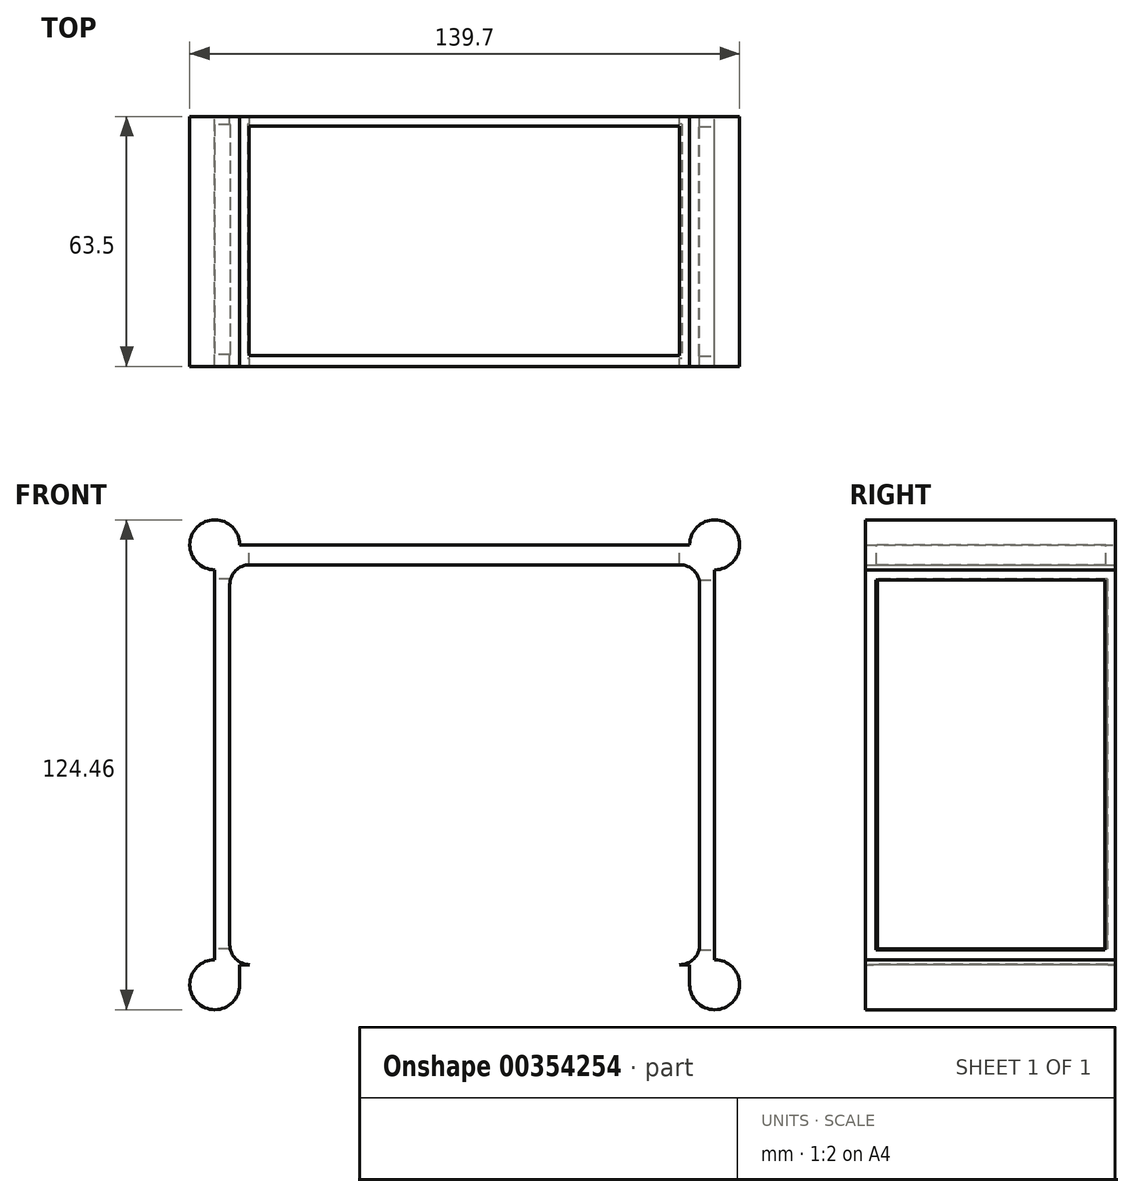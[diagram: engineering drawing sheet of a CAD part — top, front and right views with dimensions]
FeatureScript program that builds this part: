
annotation { "Feature Type Name" : "Feature", "Feature Type Description" : "" }
export const myFeature = defineFeature(function(context is Context, id is Id, definition is map)
    precondition{}
    {
        {
            var Q0;
            Q0=qCreatedBy(makeId("Front.planeOp"),FACE);
            var sketch = newSketch(context, id + "F0", { "sketchPlane" : qUnion([Q0])});
            skLineSegment(sketch, "E0", {"start": v(-62.04, -39.82) * mm, "end": v(64.96, -39.82) * mm});
            skCircle(sketch, "E1", {"center": v(-62.04, -39.82) * mm, "radius": 6.35 * mm});
            skCircle(sketch, "E2", {"center": v(64.96, -39.82) * mm, "radius": 6.35 * mm});
            skLineSegment(sketch, "E3", {"start": v(-62.04, -39.82) * mm, "end": v(-62.04, 71.94) * mm});
            skLineSegment(sketch, "E4", {"start": v(64.96, -39.82) * mm, "end": v(64.96, 71.94) * mm});
            skLineSegment(sketch, "E5", {"start": v(-62.04, 71.94) * mm, "end": v(64.96, 71.94) * mm});
            skCircle(sketch, "E6", {"center": v(-62.04, 71.94) * mm, "radius": 6.35 * mm});
            skCircle(sketch, "E7", {"center": v(64.96, 71.94) * mm, "radius": 6.35 * mm});
            skPoint(sketch, "E8.middle", {"position": v(0, 0) * mm});
            skPoint(sketch, "E9.middle", {"position": v(56.68, 68.54) * mm});
            skLineSegment(sketch, "E10.bottom", {"start": v(-58.23, 66.86) * mm, "end": v(61.15, 66.86) * mm});
            skLineSegment(sketch, "E10.top", {"start": v(-58.23, -34.74) * mm, "end": v(61.15, -34.74) * mm});
            skLineSegment(sketch, "E10.left", {"start": v(-58.23, 66.86) * mm, "end": v(-58.23, -34.74) * mm});
            skLineSegment(sketch, "E10.right", {"start": v(61.15, 66.86) * mm, "end": v(61.15, -34.74) * mm});
            skSolve(sketch);
        }
        {
            var Q0;
            Q0 = qSketchRegion(id + "F0", true);
            extrude(context, id + "F1", {"entities" : qUnion([Q0]), "depth" : 63.5 * mm});
        }
        {
            var Q0;
            Q0=makeQuery(id+"F1.opExtrude","SWEPT_FACE",FACE,{"disambiguationData":[OSD([sQuery(id+"F0.wireOp",EDGE,"E0")])]});
            var sketch = newSketch(context, id + "F2", { "sketchPlane" : qUnion([Q0])});
            skLineSegment(sketch, "E11.bottom", {"start": v(-53.74, 61.5) * mm, "end": v(56.64, 61.5) * mm});
            skLineSegment(sketch, "E11.top", {"start": v(-53.74, 1.95) * mm, "end": v(56.64, 1.95) * mm});
            skLineSegment(sketch, "E11.left", {"start": v(-53.74, 61.5) * mm, "end": v(-53.74, 1.95) * mm});
            skLineSegment(sketch, "E11.right", {"start": v(56.64, 61.5) * mm, "end": v(56.64, 1.95) * mm});
            skSolve(sketch);
        }
        {
            var Q0;
            Q0=makeQuery(id+"F2.imprint","IMPRINT",FACE,{"disambiguationData":[TD([[makeQuery(id+"F2.imprint","IMPRINT",EDGE,{"derivedFrom":sQuery(id+"F2.wireOp",EDGE,"E11.bottom")}),-1.0]])]});
            extrude(context, id + "F3", {"entities" : qUnion([Q0]), "operationType" : NewBodyOperationType.REMOVE, "oppositeDirection" : true, "depth" : 25.4 * mm});
        }
        {
            var Q0;
            Q0=makeQuery(id+"F1.opExtrude","SWEPT_FACE",FACE,{"disambiguationData":[OSD([sQuery(id+"F0.wireOp",EDGE,"E3")])]});
            var sketch = newSketch(context, id + "F4", { "sketchPlane" : qUnion([Q0])});
            skLineSegment(sketch, "E12.bottom", {"start": v(2.07, 63.24) * mm, "end": v(60.57, 63.24) * mm});
            skLineSegment(sketch, "E12.top", {"start": v(2.07, -30.72) * mm, "end": v(60.57, -30.72) * mm});
            skLineSegment(sketch, "E12.left", {"start": v(2.07, 63.24) * mm, "end": v(2.07, -30.72) * mm});
            skLineSegment(sketch, "E12.right", {"start": v(60.57, 63.24) * mm, "end": v(60.57, -30.72) * mm});
            skSolve(sketch);
        }
        {
            var Q0;
            Q0 = qSketchRegion(id + "F4", true);
            extrude(context, id + "F5", {"entities" : qUnion([Q0]), "operationType" : NewBodyOperationType.REMOVE, "oppositeDirection" : true, "depth" : 64.77 * mm});
        }
        {
            var Q0;
            Q0=makeQuery(id+"F1.opExtrude","SWEPT_FACE",FACE,{"disambiguationData":[OSD([sQuery(id+"F0.wireOp",EDGE,"E5")])]});
            var sketch = newSketch(context, id + "F6", { "sketchPlane" : qUnion([Q0])});
            skLineSegment(sketch, "E13.bottom", {"start": v(-53.34, -2.48) * mm, "end": v(55.96, -2.48) * mm});
            skLineSegment(sketch, "E13.top", {"start": v(-53.34, -60.77) * mm, "end": v(55.96, -60.77) * mm});
            skLineSegment(sketch, "E13.left", {"start": v(-53.34, -2.48) * mm, "end": v(-53.34, -60.77) * mm});
            skLineSegment(sketch, "E13.right", {"start": v(55.96, -2.48) * mm, "end": v(55.96, -60.77) * mm});
            skSolve(sketch);
        }
        {
            var Q0;
            Q0 = qSketchRegion(id + "F6", true);
            extrude(context, id + "F7", {"entities" : qUnion([Q0]), "operationType" : NewBodyOperationType.REMOVE, "oppositeDirection" : true, "depth" : 52.83 * mm});
        }
        {
            var Q0;
            Q0=makeQuery(id+"F1.opExtrude","SWEPT_FACE",FACE,{"disambiguationData":[OSD([sQuery(id+"F0.wireOp",EDGE,"E4")])]});
            var sketch = newSketch(context, id + "F8", { "sketchPlane" : qUnion([Q0])});
            skLineSegment(sketch, "E14.bottom", {"start": v(-60.87, 62.95) * mm, "end": v(-2.66, 62.95) * mm});
            skLineSegment(sketch, "E14.top", {"start": v(-60.87, -31.01) * mm, "end": v(-2.66, -31.01) * mm});
            skLineSegment(sketch, "E14.left", {"start": v(-60.87, 62.95) * mm, "end": v(-60.87, -31.01) * mm});
            skLineSegment(sketch, "E14.right", {"start": v(-2.66, 62.95) * mm, "end": v(-2.66, -31.01) * mm});
            skSolve(sketch);
        }
        {
            var Q0;
            Q0 = qSketchRegion(id + "F8", true);
            extrude(context, id + "F9", {"entities" : qUnion([Q0]), "operationType" : NewBodyOperationType.REMOVE, "oppositeDirection" : true, "depth" : 43.43 * mm});
        }
        {
            var Q0;
            Q0=makeQuery(id+"F1.opExtrude","SWEPT_EDGE",EDGE,{"disambiguationData":[OSD([sQuery(id+"F0.wireOp",EDGE,"E7"),sQuery(id+"F0.wireOp",EDGE,"E10.bottom"),sQuery(id+"F0.wireOp",EDGE,"E10.right")])]});
            var Q1;
            Q1=makeQuery(id+"F1.opExtrude","SWEPT_EDGE",EDGE,{"disambiguationData":[OSD([sQuery(id+"F0.wireOp",EDGE,"E6"),sQuery(id+"F0.wireOp",EDGE,"E10.bottom"),sQuery(id+"F0.wireOp",EDGE,"E10.left")])]});
            var Q2;
            Q2=makeQuery(id+"F1.opExtrude","SWEPT_EDGE",EDGE,{"disambiguationData":[OSD([sQuery(id+"F0.wireOp",EDGE,"E2"),sQuery(id+"F0.wireOp",EDGE,"E10.top"),sQuery(id+"F0.wireOp",EDGE,"E10.right")])]});
            var Q3;
            Q3=makeQuery(id+"F1.opExtrude","SWEPT_EDGE",EDGE,{"disambiguationData":[OSD([sQuery(id+"F0.wireOp",EDGE,"E1"),sQuery(id+"F0.wireOp",EDGE,"E10.top"),sQuery(id+"F0.wireOp",EDGE,"E10.left")])]});
            fillet(context, id + "F10", {"entities" : qUnion([Q0, Q1, Q2, Q3]), "radius" : 5.08 * mm, "tangentPropagation" : true, "allowEdgeOverflow" : false});
        }
        {
            var Q0;
            Q0=makeQuery(id+"F1.opExtrude","CAP_FACE",FACE,{"disambiguationData":[OSD([sQuery(id+"F0.wireOp",EDGE,"E0"),sQuery(id+"F0.wireOp",EDGE,"E1"),sQuery(id+"F0.wireOp",EDGE,"E2"),sQuery(id+"F0.wireOp",EDGE,"E3"),sQuery(id+"F0.wireOp",EDGE,"E4"),sQuery(id+"F0.wireOp",EDGE,"E5"),sQuery(id+"F0.wireOp",EDGE,"E6"),sQuery(id+"F0.wireOp",EDGE,"E7"),sQuery(id+"F0.wireOp",EDGE,"E10.bottom"),sQuery(id+"F0.wireOp",EDGE,"E10.top"),sQuery(id+"F0.wireOp",EDGE,"E10.left"),sQuery(id+"F0.wireOp",EDGE,"E10.right")])],"isStart":false});
            var sketch = newSketch(context, id + "F11", { "sketchPlane" : qUnion([Q0])});
            skLineSegment(sketch, "E15.bottom", {"start": v(-55.7, -39.82) * mm, "end": v(58.6, -39.82) * mm});
            skLineSegment(sketch, "E15.top", {"start": v(-55.7, -34.74) * mm, "end": v(58.6, -34.74) * mm});
            skLineSegment(sketch, "E15.left", {"start": v(-55.7, -39.82) * mm, "end": v(-55.7, -34.74) * mm});
            skLineSegment(sketch, "E15.right", {"start": v(58.6, -39.82) * mm, "end": v(58.6, -34.74) * mm});
            skSolve(sketch);
        }
        {
            var Q0;
            Q0 = qSketchRegion(id + "F11", true);
            extrude(context, id + "F12", {"entities" : qUnion([Q0]), "operationType" : NewBodyOperationType.REMOVE, "oppositeDirection" : true, "depth" : 127.25 * mm});
        }
    });
